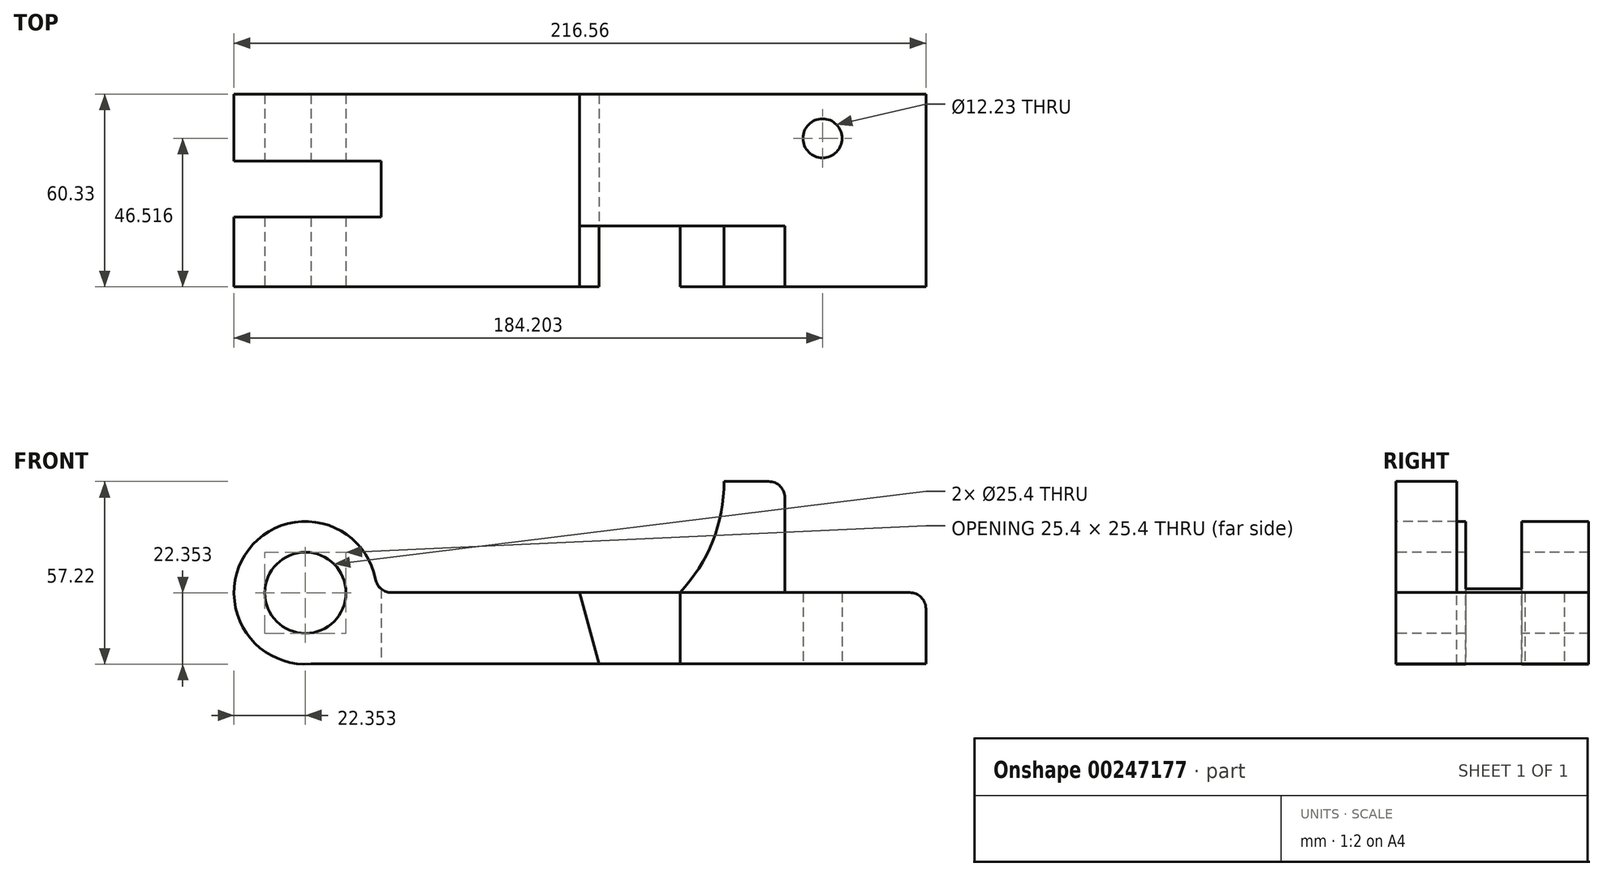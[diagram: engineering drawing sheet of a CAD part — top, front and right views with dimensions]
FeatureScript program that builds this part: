
annotation { "Feature Type Name" : "Feature", "Feature Type Description" : "" }
export const myFeature = defineFeature(function(context is Context, id is Id, definition is map)
    precondition{}
    {
        {
            var Q0;
            Q0=qCreatedBy(makeId("Front.planeOp"),FACE);
            var sketch = newSketch(context, id + "F0", { "sketchPlane" : qUnion([Q0])});
            skArc(sketch, "E0", {"start": v(-85.3, 13.05) * mm, "mid": v(-124.08, 28.14) * mm, "end": v(-105.93, -9.3) * mm});
            skLineSegment(sketch, "E1.bottom", {"start": v(-105.93, -9.3) * mm, "end": v(86.55, -9.3) * mm});
            skLineSegment(sketch, "E1.top", {"start": v(-85.3, 13.05) * mm, "end": v(9.59, 13.05) * mm});
            skLineSegment(sketch, "E1.right", {"start": v(86.55, -9.3) * mm, "end": v(86.55, 13.05) * mm});
            skLineSegment(sketch, "E2.top", {"start": v(23.38, 47.85) * mm, "end": v(37.35, 47.85) * mm});
            skLineSegment(sketch, "E2.right", {"start": v(42.43, 13.05) * mm, "end": v(42.43, 42.77) * mm});
            skLineSegment(sketch, "E3.trimOffspring", {"start": v(42.43, 13.05) * mm, "end": v(86.55, 13.05) * mm});
            skLineSegment(sketch, "E4", {"start": v(9.59, 13.05) * mm, "end": v(9.59, -9.3) * mm});
            skLineSegment(sketch, "E5", {"start": v(-15.81, -9.3) * mm, "end": v(-21.8, 13.05) * mm});
            skPoint(sketch, "E6.visualSharp", {"position": v(42.43, 47.85) * mm});
            skArc(sketch, "E6.filletArc", {"start": v(42.43, 42.77) * mm, "mid": v(40.94, 46.36) * mm, "end": v(37.35, 47.85) * mm});
            skArc(sketch, "E7", {"start": v(9.59, 13.05) * mm, "mid": v(19.8, 29.13) * mm, "end": v(23.38, 47.85) * mm});
            skCircle(sketch, "E8", {"center": v(-107.66, 12.98) * mm, "radius": 12.7 * mm});
            skLineSegment(sketch, "E9", {"start": v(9.59, 13.05) * mm, "end": v(42.43, 13.05) * mm});
            skSolve(sketch);
        }
        {
            var Q0;
            {var subQ3=sQuery(id+"F0.wireOp",EDGE,"E0");Q0=makeQuery(id+"F0.imprint","IMPRINT",FACE,{"disambiguationData":[TD([[makeQuery(id+"F0.imprint","IMPRINT",EDGE,{"derivedFrom":subQ3}),1.0]])]});}
            extrude(context, id + "F1", {"entities" : qUnion([Q0]), "oppositeDirection" : true, "depth" : 60.32 * mm});
        }
        {
            var Q0;
            {var subQ0=sQuery(id+"F0.wireOp",EDGE,"E4");Q0=makeQuery(id+"F0.imprint","IMPRINT",FACE,{"disambiguationData":[TD([[makeQuery(id+"F0.imprint","IMPRINT",EDGE,{"derivedFrom":subQ0}),-1.0]])]});}
            var Q1;
            {var subQ1=sQuery(id+"F0.wireOp",EDGE,"E1.right");Q1=makeQuery(id+"F0.imprint","IMPRINT",FACE,{"disambiguationData":[TD([[makeQuery(id+"F0.imprint","IMPRINT",EDGE,{"derivedFrom":subQ1}),1.0]])]});}
            extrude(context, id + "F2", {"entities" : qUnion([Q0, Q1]), "oppositeDirection" : true, "depth" : 60.32 * mm});
        }
        {
            var Q0;
            Q0=makeQuery(id+"F0.imprint","IMPRINT",FACE,{"disambiguationData":[TD([[makeQuery(id+"F0.imprint","IMPRINT",EDGE,{"derivedFrom":sQuery(id+"F0.wireOp",EDGE,"E2.top")}),-1.0]])]});
            extrude(context, id + "F3", {"entities" : qUnion([Q0]), "oppositeDirection" : true, "depth" : 19.05 * mm});
        }
        {
            var Q0;
            {var subQ0=sQuery(id+"F0.wireOp",EDGE,"E4");Q0=makeQuery(id+"F0.imprint","IMPRINT",FACE,{"disambiguationData":[TD([[makeQuery(id+"F0.imprint","IMPRINT",EDGE,{"derivedFrom":subQ0}),-1.0]])]});}
            extrude(context, id + "F4", {"entities" : qUnion([Q0]), "operationType" : NewBodyOperationType.REMOVE, "oppositeDirection" : true, "depth" : 19.05 * mm});
        }
        {
            var Q0;
            Q0=makeQuery(id+"F2.opExtrude","SWEPT_FACE",FACE,{"disambiguationData":[OSD([sQuery(id+"F0.wireOp",EDGE,"E1.top"),sQuery(id+"F0.wireOp",EDGE,"E3.trimOffspring"),sQuery(id+"F0.wireOp",EDGE,"E9")])]});
            var sketch = newSketch(context, id + "F5", { "sketchPlane" : qUnion([Q0])});
            skCircle(sketch, "E10", {"center": v(54.2, 46.52) * mm, "radius": 6.12 * mm});
            skLineSegment(sketch, "E11.bottom", {"start": v(-133.85, 39.38) * mm, "end": v(-83.9, 39.38) * mm});
            skLineSegment(sketch, "E11.top", {"start": v(-133.85, 21.8) * mm, "end": v(-83.9, 21.8) * mm});
            skLineSegment(sketch, "E11.left", {"start": v(-133.85, 39.38) * mm, "end": v(-133.85, 21.8) * mm});
            skLineSegment(sketch, "E11.right", {"start": v(-83.9, 39.38) * mm, "end": v(-83.9, 21.8) * mm});
            skSolve(sketch);
        }
        {
            var Q0;
            Q0=makeQuery(id+"F5.imprint","IMPRINT",FACE,{"disambiguationData":[TD([[makeQuery(id+"F5.imprint","IMPRINT",EDGE,{"derivedFrom":sQuery(id+"F5.wireOp",EDGE,"E11.bottom")}),-1.0]])]});
            var Q1;
            Q1=makeQuery(id+"F5.imprint","IMPRINT",FACE,{"disambiguationData":[TD([[makeQuery(id+"F5.imprint","IMPRINT",EDGE,{"derivedFrom":sQuery(id+"F5.wireOp",EDGE,"E10")}),1.0]])]});
            extrude(context, id + "F6", {"entities" : qUnion([Q0, Q1]), "operationType" : NewBodyOperationType.REMOVE, "endBound" : BoundingType.THROUGH_ALL, "depth" : 25.4 * mm, "hasSecondDirection" : true, "secondDirectionOppositeDirection" : true, "secondDirectionDepth" : 25.4 * mm});
        }
        {
            var Q0;
            {var subQ0=sQuery(id+"F0.wireOp",EDGE,"E0");var subQ1=sQuery(id+"F0.wireOp",EDGE,"E1.top");Q0=makeQuery(id+"F6.boolean.opBoolean","SPLIT",EDGE,{"disambiguationData":[TD([makeQuery(id+"F6.opExtrude","SWEPT_FACE",FACE,{"disambiguationData":[OSD([sQuery(id+"F5.wireOp",EDGE,"E11.top")])]})])],"derivedFrom":makeQuery(id+"F1.opExtrude","SWEPT_EDGE",EDGE,{"disambiguationData":[OSD([subQ0,subQ1])]})});}
            fillet(context, id + "F7", {"entities" : qUnion([Q0]), "radius" : 5.08 * mm, "tangentPropagation" : true, "allowEdgeOverflow" : false});
        }
        {
            var Q0;
            Q0=makeQuery(id+"F2.opExtrude","SWEPT_EDGE",EDGE,{"disambiguationData":[OSD([sQuery(id+"F0.wireOp",EDGE,"E1.right"),sQuery(id+"F0.wireOp",EDGE,"E3.trimOffspring")])]});
            fillet(context, id + "F8", {"entities" : qUnion([Q0]), "radius" : 5.08 * mm, "tangentPropagation" : true, "allowEdgeOverflow" : false});
        }
    });
